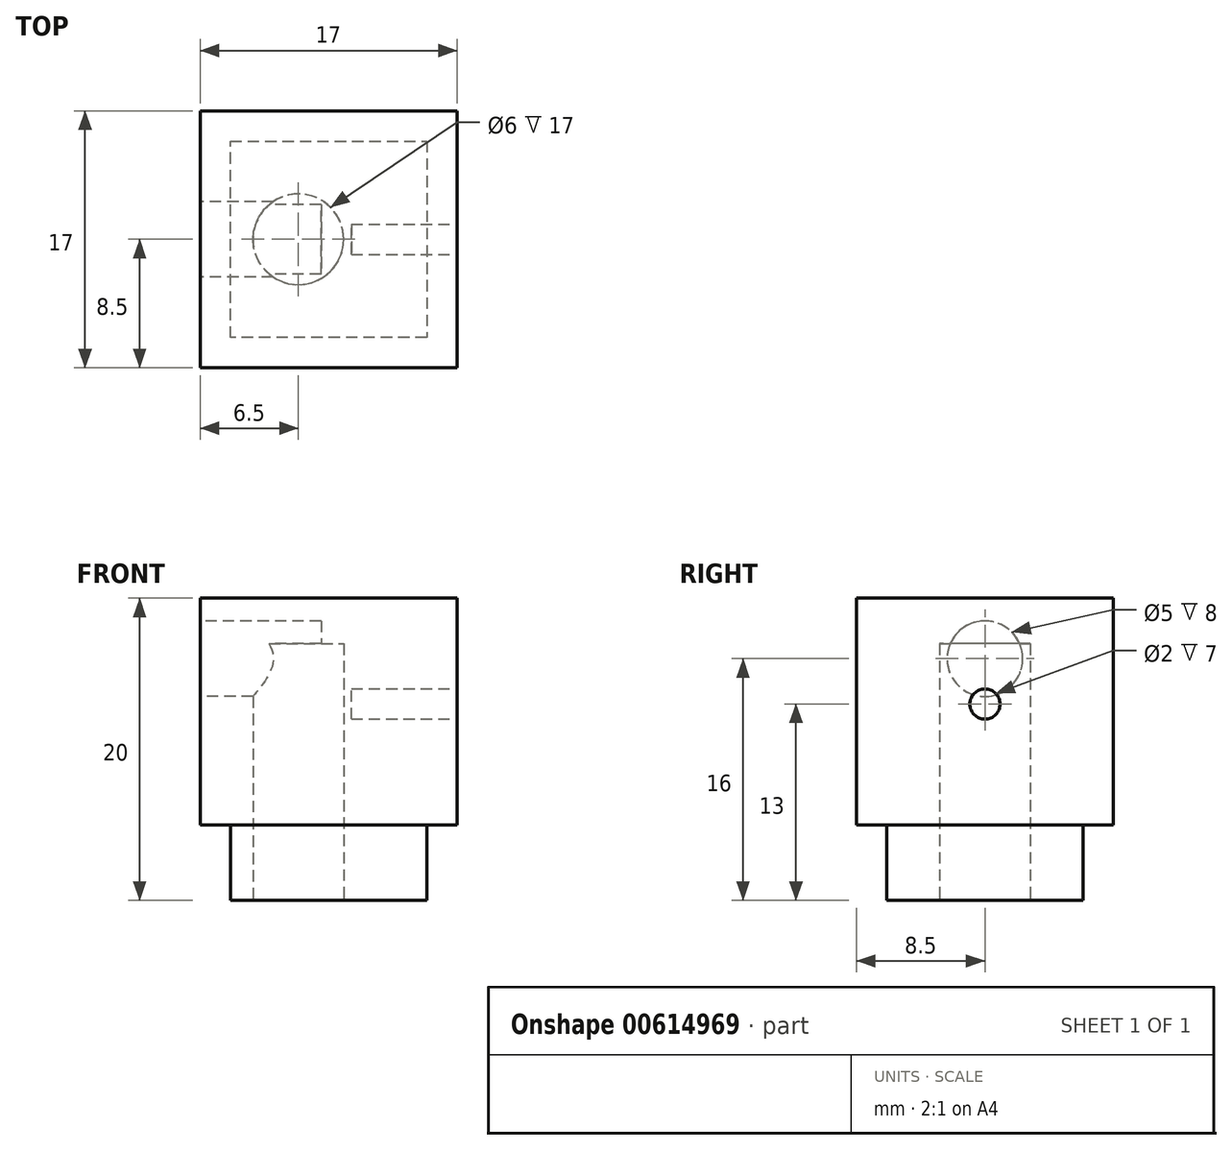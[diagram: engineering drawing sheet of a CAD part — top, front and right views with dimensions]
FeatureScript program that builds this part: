
annotation { "Feature Type Name" : "Feature", "Feature Type Description" : "" }
export const myFeature = defineFeature(function(context is Context, id is Id, definition is map)
    precondition{}
    {
        {
            var Q0;
            Q0=qCreatedBy(makeId("Top.planeOp"),FACE);
            var sketch = newSketch(context, id + "F0", { "sketchPlane" : qUnion([Q0])});
            skLineSegment(sketch, "E0", {"start": v(0, 0) * mm, "end": v(0, 13) * mm});
            skLineSegment(sketch, "E1", {"start": v(0, 13) * mm, "end": v(13, 13) * mm});
            skLineSegment(sketch, "E2", {"start": v(13, 13) * mm, "end": v(13, 0) * mm});
            skLineSegment(sketch, "E3", {"start": v(13, 0) * mm, "end": v(0, 0) * mm});
            skSolve(sketch);
        }
        {
            var Q0;
            Q0=makeQuery(id+"F0.imprint","IMPRINT",FACE,{"disambiguationData":[TD([[makeQuery(id+"F0.imprint","IMPRINT",EDGE,{"derivedFrom":sQuery(id+"F0.wireOp",EDGE,"E0")}),-1.0]])]});
            extrude(context, id + "F1", {"entities" : qUnion([Q0]), "depth" : 20 * mm, "offsetDistance" : 25 * mm});
        }
        {
            var Q0;
            Q0=makeQuery(id+"F1.opExtrude","CAP_FACE",FACE,{"disambiguationData":[OSD([sQuery(id+"F0.wireOp",EDGE,"E0"),sQuery(id+"F0.wireOp",EDGE,"E1"),sQuery(id+"F0.wireOp",EDGE,"E2"),sQuery(id+"F0.wireOp",EDGE,"E3")])],"isStart":false});
            var sketch = newSketch(context, id + "F2", { "sketchPlane" : qUnion([Q0])});
            skLineSegment(sketch, "E4", {"start": v(0, 0) * mm, "end": v(-2, 0) * mm});
            skLineSegment(sketch, "E5", {"start": v(-2, 0) * mm, "end": v(-2, -2) * mm});
            skLineSegment(sketch, "E6", {"start": v(-2, -2) * mm, "end": v(15, -2) * mm});
            skLineSegment(sketch, "E7", {"start": v(15, -2) * mm, "end": v(15, 15) * mm});
            skLineSegment(sketch, "E8", {"start": v(15, 15) * mm, "end": v(-2, 15) * mm});
            skLineSegment(sketch, "E9", {"start": v(-2, 15) * mm, "end": v(-2, -2) * mm});
            skSolve(sketch);
        }
        {
            var Q0;
            {var subQ3=sQuery(id+"F2.wireOp",EDGE,"E6");Q0=makeQuery(id+"F2.imprint","IMPRINT",FACE,{"disambiguationData":[TD([[makeQuery(id+"F2.imprint","IMPRINT",EDGE,{"derivedFrom":subQ3}),1.0]])]});}
            extrude(context, id + "F3", {"entities" : qUnion([Q0]), "operationType" : NewBodyOperationType.ADD, "oppositeDirection" : true, "depth" : 15 * mm, "offsetDistance" : 25 * mm});
        }
        {
            var Q0;
            Q0=makeQuery(id+"F3.opExtrude","SWEPT_FACE",FACE,{"disambiguationData":[OSD([sQuery(id+"F2.wireOp",EDGE,"E7")])]});
            var sketch = newSketch(context, id + "F4", { "sketchPlane" : qUnion([Q0])});
            skLineSegment(sketch, "E10", {"start": v(15, 20) * mm, "end": v(6.5, 20) * mm});
            skLineSegment(sketch, "E11", {"start": v(6.5, 20) * mm, "end": v(6.5, 13) * mm});
            skCircle(sketch, "E12", {"center": v(6.5, 13) * mm, "radius": 1 * mm});
            skSolve(sketch);
        }
        {
            var Q0;
            Q0=makeQuery(id+"F4.imprint","IMPRINT",FACE,{"disambiguationData":[TD([[makeQuery(id+"F4.imprint","IMPRINT",EDGE,{"derivedFrom":sQuery(id+"F4.wireOp",EDGE,"E12")}),1.0]])]});
            extrude(context, id + "F5", {"entities" : qUnion([Q0]), "operationType" : NewBodyOperationType.REMOVE, "oppositeDirection" : true, "depth" : 7 * mm, "offsetDistance" : 25 * mm});
        }
        {
            var Q0;
            Q0=makeQuery(id+"F3.opExtrude","SWEPT_FACE",FACE,{"disambiguationData":[OSD([sQuery(id+"F2.wireOp",EDGE,"E9")])]});
            var sketch = newSketch(context, id + "F6", { "sketchPlane" : qUnion([Q0])});
            skLineSegment(sketch, "E13", {"start": v(-15, 20) * mm, "end": v(-6.5, 20) * mm});
            skLineSegment(sketch, "E14", {"start": v(-6.5, 20) * mm, "end": v(-6.5, 16) * mm});
            skCircle(sketch, "E15", {"center": v(-6.5, 16) * mm, "radius": 2.5 * mm});
            skSolve(sketch);
        }
        {
            var Q0;
            Q0=makeQuery(id+"F6.imprint","IMPRINT",FACE,{"disambiguationData":[TD([[makeQuery(id+"F6.imprint","IMPRINT",EDGE,{"derivedFrom":sQuery(id+"F6.wireOp",EDGE,"E15")}),1.0]])]});
            extrude(context, id + "F7", {"entities" : qUnion([Q0]), "operationType" : NewBodyOperationType.REMOVE, "oppositeDirection" : true, "depth" : 8 * mm, "offsetDistance" : 25 * mm});
        }
        {
            var Q0;
            Q0=makeQuery(id+"F1.opExtrude","CAP_FACE",FACE,{"disambiguationData":[OSD([sQuery(id+"F0.wireOp",EDGE,"E0"),sQuery(id+"F0.wireOp",EDGE,"E1"),sQuery(id+"F0.wireOp",EDGE,"E2"),sQuery(id+"F0.wireOp",EDGE,"E3")])],"isStart":true});
            var sketch = newSketch(context, id + "F8", { "sketchPlane" : qUnion([Q0])});
            skLineSegment(sketch, "E16", {"start": v(0, -13) * mm, "end": v(0, -6.5) * mm});
            skLineSegment(sketch, "E17", {"start": v(0, -6.5) * mm, "end": v(4.5, -6.5) * mm});
            skCircle(sketch, "E18", {"center": v(4.5, -6.5) * mm, "radius": 3 * mm});
            skSolve(sketch);
        }
        {
            var Q0;
            Q0=makeQuery(id+"F8.imprint","IMPRINT",FACE,{"disambiguationData":[TD([[makeQuery(id+"F8.imprint","IMPRINT",EDGE,{"derivedFrom":sQuery(id+"F8.wireOp",EDGE,"E18")}),1.0]])]});
            extrude(context, id + "F9", {"entities" : qUnion([Q0]), "operationType" : NewBodyOperationType.REMOVE, "oppositeDirection" : true, "depth" : 17 * mm, "offsetDistance" : 25 * mm});
        }
    });
